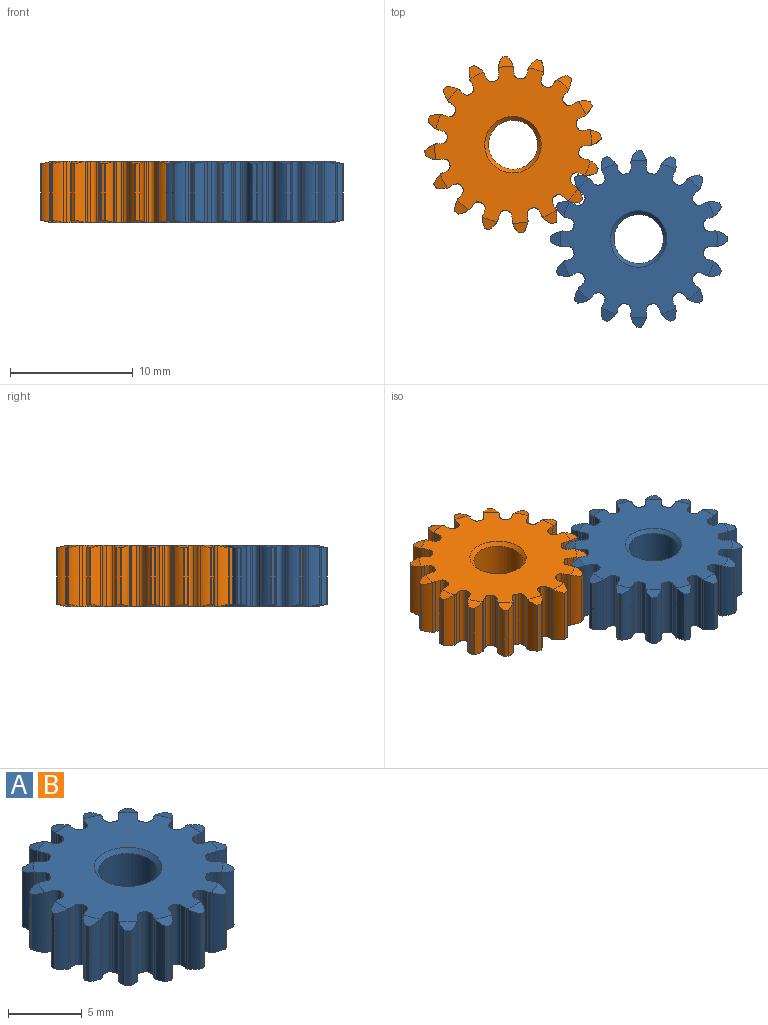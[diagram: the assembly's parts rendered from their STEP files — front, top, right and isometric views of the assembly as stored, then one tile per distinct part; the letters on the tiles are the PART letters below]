
ASSEMBLY  parts=2 mates=1
PART A: 229 faces, bbox 14.4x14.4x5 mm
  f0: plane 12.8x12.8mm, normal (0,0,-1), area 96.1mm2, adj f1,f2,f3,f4,f5,f6,f7,f8
  f1: cone r=9.2mm half-angle=75deg, axis (0,0,1), area 0.7mm2, adj f0,f17,f63,f64,f65,f208
  f2: cone r=9.2mm half-angle=75deg, axis (0,0,1), area 0.7mm2, adj f0,f60,f61,f62,f199,f200
  f3: cone r=9.2mm half-angle=75deg, axis (0,0,1), area 0.7mm2, adj f0,f57,f58,f59,f190,f191
  f4: cone r=9.2mm half-angle=75deg, axis (0,0,1), area 0.7mm2, adj f0,f54,f55,f56,f181,f182
  f5: cone r=9.2mm half-angle=75deg, axis (0,0,1), area 0.7mm2, adj f0,f51,f52,f53,f172,f173
  f6: cone r=9.2mm half-angle=75deg, axis (0,0,1), area 0.7mm2, adj f0,f48,f49,f50,f163,f164
  f7: cone r=9.2mm half-angle=75deg, axis (0,0,1), area 0.7mm2, adj f0,f45,f46,f47,f154,f155
  f8: cone r=9.2mm half-angle=75deg, axis (0,0,1), area 0.7mm2, adj f0,f42,f43,f44,f145,f146
  f9: cone r=9.2mm half-angle=75deg, axis (0,0,1), area 0.7mm2, adj f0,f39,f40,f41,f136,f137
  f10: cone r=9.2mm half-angle=75deg, axis (0,0,1), area 0.7mm2, adj f0,f36,f37,f38,f127,f128
  f11: cone r=9.2mm half-angle=75deg, axis (0,0,1), area 0.7mm2, adj f0,f33,f34,f35,f118,f119
  f12: cone r=9.2mm half-angle=75deg, axis (0,0,1), area 0.7mm2, adj f0,f30,f31,f32,f109,f110
  f13: cone r=9.2mm half-angle=75deg, axis (0,0,1), area 0.7mm2, adj f0,f27,f28,f29,f100,f101
  f14: cone r=9.2mm half-angle=75deg, axis (0,0,1), area 0.7mm2, adj f0,f24,f25,f26,f91,f92
  f15: cone r=9.2mm half-angle=75deg, axis (0,0,1), area 0.7mm2, adj f0,f21,f22,f23,f82,f83
  f16: cone r=9.2mm half-angle=75deg, axis (0,0,1), area 0.7mm2, adj f0,f18,f19,f20,f73,f74
  f17: cylinder r=0.08mm len=4.59mm, axis (0,0,-1), area 0.3mm2, adj f1,f64,f65,f225
  f18: cylinder r=0.08mm len=4.59mm, axis (0,0,-1), area 0.3mm2, adj f16,f19,f73,f210
  f19: cylinder r=7.2mm len=4.57mm, axis (0,0,-1), area 1.4mm2, adj f16,f18,f20,f210
  f20: cylinder r=0.08mm len=4.59mm, axis (0,0,-1), area 0.3mm2, adj f16,f19,f74,f210
  f21: cylinder r=0.08mm len=4.59mm, axis (0,0,-1), area 0.3mm2, adj f15,f22,f82,f211
  f22: cylinder r=7.2mm len=4.57mm, axis (0,0,-1), area 1.4mm2, adj f15,f21,f23,f211
  f23: cylinder r=0.08mm len=4.59mm, axis (0,0,-1), area 0.3mm2, adj f15,f22,f83,f211
  f24: cylinder r=0.08mm len=4.59mm, axis (0,0,-1), area 0.3mm2, adj f14,f25,f91,f212
  f25: cylinder r=7.2mm len=4.57mm, axis (0,0,-1), area 1.4mm2, adj f14,f24,f26,f212
  f26: cylinder r=0.08mm len=4.59mm, axis (0,0,-1), area 0.3mm2, adj f14,f25,f92,f212
  f27: cylinder r=0.08mm len=4.59mm, axis (0,0,-1), area 0.3mm2, adj f13,f28,f100,f213
  f28: cylinder r=7.2mm len=4.57mm, axis (0,0,-1), area 1.4mm2, adj f13,f27,f29,f213
  f29: cylinder r=0.08mm len=4.59mm, axis (0,0,-1), area 0.3mm2, adj f13,f28,f101,f213
  f30: cylinder r=0.08mm len=4.59mm, axis (0,0,-1), area 0.3mm2, adj f12,f31,f109,f214
  f31: cylinder r=7.2mm len=4.57mm, axis (0,0,-1), area 1.4mm2, adj f12,f30,f32,f214
  f32: cylinder r=0.08mm len=4.59mm, axis (0,0,-1), area 0.3mm2, adj f12,f31,f110,f214
  f33: cylinder r=0.08mm len=4.59mm, axis (0,0,-1), area 0.3mm2, adj f11,f34,f118,f215
  f34: cylinder r=7.2mm len=4.57mm, axis (0,0,-1), area 1.4mm2, adj f11,f33,f35,f215
  f35: cylinder r=0.08mm len=4.59mm, axis (0,0,-1), area 0.3mm2, adj f11,f34,f119,f215
  f36: cylinder r=0.08mm len=4.59mm, axis (0,0,-1), area 0.3mm2, adj f10,f37,f127,f216
  f37: cylinder r=7.2mm len=4.57mm, axis (0,0,-1), area 1.4mm2, adj f10,f36,f38,f216
  f38: cylinder r=0.08mm len=4.59mm, axis (0,0,-1), area 0.3mm2, adj f10,f37,f128,f216
  f39: cylinder r=0.08mm len=4.59mm, axis (0,0,-1), area 0.3mm2, adj f9,f40,f136,f217
  f40: cylinder r=7.2mm len=4.57mm, axis (0,0,-1), area 1.4mm2, adj f9,f39,f41,f217
  f41: cylinder r=0.08mm len=4.59mm, axis (0,0,-1), area 0.3mm2, adj f9,f40,f137,f217
  f42: cylinder r=0.08mm len=4.59mm, axis (0,0,-1), area 0.3mm2, adj f8,f43,f145,f218
  f43: cylinder r=7.2mm len=4.57mm, axis (0,0,-1), area 1.4mm2, adj f8,f42,f44,f218
  f44: cylinder r=0.08mm len=4.59mm, axis (0,0,-1), area 0.3mm2, adj f8,f43,f146,f218
  f45: cylinder r=0.08mm len=4.59mm, axis (0,0,-1), area 0.3mm2, adj f7,f46,f154,f219
  f46: cylinder r=7.2mm len=4.57mm, axis (0,0,-1), area 1.4mm2, adj f7,f45,f47,f219
  f47: cylinder r=0.08mm len=4.59mm, axis (0,0,-1), area 0.3mm2, adj f7,f46,f155,f219
  f48: cylinder r=0.08mm len=4.59mm, axis (0,0,-1), area 0.3mm2, adj f6,f49,f163,f220
  f49: cylinder r=7.2mm len=4.57mm, axis (0,0,-1), area 1.4mm2, adj f6,f48,f50,f220
  f50: cylinder r=0.08mm len=4.59mm, axis (0,0,-1), area 0.3mm2, adj f6,f49,f164,f220
  f51: cylinder r=0.08mm len=4.59mm, axis (0,0,-1), area 0.3mm2, adj f5,f52,f172,f221
  f52: cylinder r=7.2mm len=4.57mm, axis (0,0,-1), area 1.4mm2, adj f5,f51,f53,f221
  f53: cylinder r=0.08mm len=4.59mm, axis (0,0,-1), area 0.3mm2, adj f5,f52,f173,f221
  f54: cylinder r=0.08mm len=4.59mm, axis (0,0,-1), area 0.3mm2, adj f4,f55,f181,f222
  f55: cylinder r=7.2mm len=4.57mm, axis (0,0,-1), area 1.4mm2, adj f4,f54,f56,f222
  f56: cylinder r=0.08mm len=4.59mm, axis (0,0,-1), area 0.3mm2, adj f4,f55,f182,f222
  f57: cylinder r=0.08mm len=4.59mm, axis (0,0,-1), area 0.3mm2, adj f3,f58,f190,f223
  f58: cylinder r=7.2mm len=4.57mm, axis (0,0,-1), area 1.4mm2, adj f3,f57,f59,f223
  f59: cylinder r=0.08mm len=4.59mm, axis (0,0,-1), area 0.3mm2, adj f3,f58,f191,f223
  f60: cylinder r=0.08mm len=4.59mm, axis (0,0,-1), area 0.3mm2, adj f2,f61,f199,f224
  f61: cylinder r=7.2mm len=4.57mm, axis (0,0,-1), area 1.4mm2, adj f2,f60,f62,f224
  f62: cylinder r=0.08mm len=4.59mm, axis (0,0,-1), area 0.3mm2, adj f2,f61,f200,f224
  f63: cylinder r=0.08mm len=4.59mm, axis (0,0,-1), area 0.3mm2, adj f1,f64,f208,f225
  f64: cylinder r=7.2mm len=4.57mm, axis (0,0,-1), area 1.4mm2, adj f1,f17,f63,f225
  f65: cylinder r=2mm len=5mm, axis (0,0,-1), area 4.4mm2, adj f1,f17,f66,f225
  f66: cylinder r=0.65mm len=5mm, axis (0,0,-1), area 1.3mm2, adj f0,f65,f67,f209
  f67: cylinder r=1.6mm len=5mm, axis (0,0,-1), area 2.4mm2, adj f0,f66,f68,f209
  f68: cylinder r=0.4mm len=5mm, axis (0,0,-1), area 2.5mm2, adj f0,f67,f69,f209
  f69: cylinder r=5.4mm len=5mm, axis (0,0,-1), area 0.9mm2, adj f0,f68,f70,f209
  f70: cylinder r=0.4mm len=5mm, axis (0,0,-1), area 2.5mm2, adj f0,f69,f71,f209
  f71: cylinder r=1.6mm len=5mm, axis (0,0,-1), area 2.4mm2, adj f0,f70,f72,f209
  f72: cylinder r=0.65mm len=5mm, axis (0,0,-1), area 1.3mm2, adj f0,f71,f73,f209
  f73: cylinder r=2mm len=5mm, axis (0,0,-1), area 4.4mm2, adj f16,f18,f72,f210
  f74: cylinder r=2mm len=5mm, axis (0,0,-1), area 4.4mm2, adj f16,f20,f75,f210
  f75: cylinder r=0.65mm len=5mm, axis (0,0,-1), area 1.3mm2, adj f0,f74,f76,f209
  f76: cylinder r=1.6mm len=5mm, axis (0,0,-1), area 2.4mm2, adj f0,f75,f77,f209
  f77: cylinder r=0.4mm len=5mm, axis (0,0,-1), area 2.5mm2, adj f0,f76,f78,f209
  f78: cylinder r=5.4mm len=5mm, axis (0,0,-1), area 0.9mm2, adj f0,f77,f79,f209
  f79: cylinder r=0.4mm len=5mm, axis (0,0,-1), area 2.5mm2, adj f0,f78,f80,f209
  f80: cylinder r=1.6mm len=5mm, axis (0,0,-1), area 2.4mm2, adj f0,f79,f81,f209
  f81: cylinder r=0.65mm len=5mm, axis (0,0,-1), area 1.3mm2, adj f0,f80,f82,f209
  f82: cylinder r=2mm len=5mm, axis (0,0,-1), area 4.4mm2, adj f15,f21,f81,f211
  f83: cylinder r=2mm len=5mm, axis (0,0,-1), area 4.4mm2, adj f15,f23,f84,f211
  f84: cylinder r=0.65mm len=5mm, axis (0,0,-1), area 1.3mm2, adj f0,f83,f85,f209
  f85: cylinder r=1.6mm len=5mm, axis (0,0,-1), area 2.4mm2, adj f0,f84,f86,f209
  f86: cylinder r=0.4mm len=5mm, axis (0,0,-1), area 2.5mm2, adj f0,f85,f87,f209
  f87: cylinder r=5.4mm len=5mm, axis (0,0,-1), area 0.9mm2, adj f0,f86,f88,f209
  f88: cylinder r=0.4mm len=5mm, axis (0,0,-1), area 2.5mm2, adj f0,f87,f89,f209
  f89: cylinder r=1.6mm len=5mm, axis (0,0,-1), area 2.4mm2, adj f0,f88,f90,f209
  f90: cylinder r=0.65mm len=5mm, axis (0,0,-1), area 1.3mm2, adj f0,f89,f91,f209
  f91: cylinder r=2mm len=5mm, axis (0,0,-1), area 4.4mm2, adj f14,f24,f90,f212
  f92: cylinder r=2mm len=5mm, axis (0,0,-1), area 4.4mm2, adj f14,f26,f93,f212
  f93: cylinder r=0.65mm len=5mm, axis (0,0,-1), area 1.3mm2, adj f0,f92,f94,f209
  f94: cylinder r=1.6mm len=5mm, axis (0,0,-1), area 2.4mm2, adj f0,f93,f95,f209
  f95: cylinder r=0.4mm len=5mm, axis (0,0,-1), area 2.5mm2, adj f0,f94,f96,f209
  f96: cylinder r=5.4mm len=5mm, axis (0,0,-1), area 0.9mm2, adj f0,f95,f97,f209
  f97: cylinder r=0.4mm len=5mm, axis (0,0,-1), area 2.5mm2, adj f0,f96,f98,f209
  f98: cylinder r=1.6mm len=5mm, axis (0,0,-1), area 2.4mm2, adj f0,f97,f99,f209
  f99: cylinder r=0.65mm len=5mm, axis (0,0,-1), area 1.3mm2, adj f0,f98,f100,f209
  f100: cylinder r=2mm len=5mm, axis (0,0,-1), area 4.4mm2, adj f13,f27,f99,f213
  f101: cylinder r=2mm len=5mm, axis (0,0,-1), area 4.4mm2, adj f13,f29,f102,f213
  f102: cylinder r=0.65mm len=5mm, axis (0,0,-1), area 1.3mm2, adj f0,f101,f103,f209
  f103: cylinder r=1.6mm len=5mm, axis (0,0,-1), area 2.4mm2, adj f0,f102,f104,f209
  f104: cylinder r=0.4mm len=5mm, axis (0,0,-1), area 2.5mm2, adj f0,f103,f105,f209
  f105: cylinder r=5.4mm len=5mm, axis (0,0,-1), area 0.9mm2, adj f0,f104,f106,f209
  f106: cylinder r=0.4mm len=5mm, axis (0,0,-1), area 2.5mm2, adj f0,f105,f107,f209
  f107: cylinder r=1.6mm len=5mm, axis (0,0,-1), area 2.4mm2, adj f0,f106,f108,f209
  f108: cylinder r=0.65mm len=5mm, axis (0,0,-1), area 1.3mm2, adj f0,f107,f109,f209
  f109: cylinder r=2mm len=5mm, axis (0,0,-1), area 4.4mm2, adj f12,f30,f108,f214
  f110: cylinder r=2mm len=5mm, axis (0,0,-1), area 4.4mm2, adj f12,f32,f111,f214
  f111: cylinder r=0.65mm len=5mm, axis (0,0,-1), area 1.3mm2, adj f0,f110,f112,f209
  f112: cylinder r=1.6mm len=5mm, axis (0,0,-1), area 2.4mm2, adj f0,f111,f113,f209
  f113: cylinder r=0.4mm len=5mm, axis (0,0,-1), area 2.5mm2, adj f0,f112,f114,f209
  f114: cylinder r=5.4mm len=5mm, axis (0,0,-1), area 0.9mm2, adj f0,f113,f115,f209
  f115: cylinder r=0.4mm len=5mm, axis (0,0,-1), area 2.5mm2, adj f0,f114,f116,f209
  f116: cylinder r=1.6mm len=5mm, axis (0,0,-1), area 2.4mm2, adj f0,f115,f117,f209
  f117: cylinder r=0.65mm len=5mm, axis (0,0,-1), area 1.3mm2, adj f0,f116,f118,f209
  f118: cylinder r=2mm len=5mm, axis (0,0,-1), area 4.4mm2, adj f11,f33,f117,f215
  f119: cylinder r=2mm len=5mm, axis (0,0,-1), area 4.4mm2, adj f11,f35,f120,f215
  f120: cylinder r=0.65mm len=5mm, axis (0,0,-1), area 1.3mm2, adj f0,f119,f121,f209
  f121: cylinder r=1.6mm len=5mm, axis (0,0,-1), area 2.4mm2, adj f0,f120,f122,f209
  f122: cylinder r=0.4mm len=5mm, axis (0,0,-1), area 2.5mm2, adj f0,f121,f123,f209
  f123: cylinder r=5.4mm len=5mm, axis (0,0,-1), area 0.9mm2, adj f0,f122,f124,f209
  f124: cylinder r=0.4mm len=5mm, axis (0,0,-1), area 2.5mm2, adj f0,f123,f125,f209
  f125: cylinder r=1.6mm len=5mm, axis (0,0,-1), area 2.4mm2, adj f0,f124,f126,f209
  f126: cylinder r=0.65mm len=5mm, axis (0,0,-1), area 1.3mm2, adj f0,f125,f127,f209
  f127: cylinder r=2mm len=5mm, axis (0,0,-1), area 4.4mm2, adj f10,f36,f126,f216
  f128: cylinder r=2mm len=5mm, axis (0,0,-1), area 4.4mm2, adj f10,f38,f129,f216
  f129: cylinder r=0.65mm len=5mm, axis (0,0,-1), area 1.3mm2, adj f0,f128,f130,f209
  f130: cylinder r=1.6mm len=5mm, axis (0,0,-1), area 2.4mm2, adj f0,f129,f131,f209
  f131: cylinder r=0.4mm len=5mm, axis (0,0,-1), area 2.5mm2, adj f0,f130,f132,f209
  f132: cylinder r=5.4mm len=5mm, axis (0,0,-1), area 0.9mm2, adj f0,f131,f133,f209
  f133: cylinder r=0.4mm len=5mm, axis (0,0,-1), area 2.5mm2, adj f0,f132,f134,f209
  f134: cylinder r=1.6mm len=5mm, axis (0,0,-1), area 2.4mm2, adj f0,f133,f135,f209
  f135: cylinder r=0.65mm len=5mm, axis (0,0,-1), area 1.3mm2, adj f0,f134,f136,f209
  f136: cylinder r=2mm len=5mm, axis (0,0,-1), area 4.4mm2, adj f9,f39,f135,f217
  f137: cylinder r=2mm len=5mm, axis (0,0,-1), area 4.4mm2, adj f9,f41,f138,f217
  f138: cylinder r=0.65mm len=5mm, axis (0,0,-1), area 1.3mm2, adj f0,f137,f139,f209
  f139: cylinder r=1.6mm len=5mm, axis (0,0,-1), area 2.4mm2, adj f0,f138,f140,f209
  f140: cylinder r=0.4mm len=5mm, axis (0,0,-1), area 2.5mm2, adj f0,f139,f141,f209
  f141: cylinder r=5.4mm len=5mm, axis (0,0,-1), area 0.9mm2, adj f0,f140,f142,f209
  f142: cylinder r=0.4mm len=5mm, axis (0,0,-1), area 2.5mm2, adj f0,f141,f143,f209
  f143: cylinder r=1.6mm len=5mm, axis (0,0,-1), area 2.4mm2, adj f0,f142,f144,f209
  f144: cylinder r=0.65mm len=5mm, axis (0,0,-1), area 1.3mm2, adj f0,f143,f145,f209
  f145: cylinder r=2mm len=5mm, axis (0,0,-1), area 4.4mm2, adj f8,f42,f144,f218
  f146: cylinder r=2mm len=5mm, axis (0,0,-1), area 4.4mm2, adj f8,f44,f147,f218
  f147: cylinder r=0.65mm len=5mm, axis (0,0,-1), area 1.3mm2, adj f0,f146,f148,f209
  f148: cylinder r=1.6mm len=5mm, axis (0,0,-1), area 2.4mm2, adj f0,f147,f149,f209
  f149: cylinder r=0.4mm len=5mm, axis (0,0,-1), area 2.5mm2, adj f0,f148,f150,f209
  f150: cylinder r=5.4mm len=5mm, axis (0,0,-1), area 0.9mm2, adj f0,f149,f151,f209
  f151: cylinder r=0.4mm len=5mm, axis (0,0,-1), area 2.5mm2, adj f0,f150,f152,f209
  f152: cylinder r=1.6mm len=5mm, axis (0,0,-1), area 2.4mm2, adj f0,f151,f153,f209
  f153: cylinder r=0.65mm len=5mm, axis (0,0,-1), area 1.3mm2, adj f0,f152,f154,f209
  f154: cylinder r=2mm len=5mm, axis (0,0,-1), area 4.4mm2, adj f7,f45,f153,f219
  f155: cylinder r=2mm len=5mm, axis (0,0,-1), area 4.4mm2, adj f7,f47,f156,f219
  f156: cylinder r=0.65mm len=5mm, axis (0,0,-1), area 1.3mm2, adj f0,f155,f157,f209
  f157: cylinder r=1.6mm len=5mm, axis (0,0,-1), area 2.4mm2, adj f0,f156,f158,f209
  f158: cylinder r=0.4mm len=5mm, axis (0,0,-1), area 2.5mm2, adj f0,f157,f159,f209
  f159: cylinder r=5.4mm len=5mm, axis (0,0,-1), area 0.9mm2, adj f0,f158,f160,f209
  f160: cylinder r=0.4mm len=5mm, axis (0,0,-1), area 2.5mm2, adj f0,f159,f161,f209
  f161: cylinder r=1.6mm len=5mm, axis (0,0,-1), area 2.4mm2, adj f0,f160,f162,f209
  f162: cylinder r=0.65mm len=5mm, axis (0,0,-1), area 1.3mm2, adj f0,f161,f163,f209
  f163: cylinder r=2mm len=5mm, axis (0,0,-1), area 4.4mm2, adj f6,f48,f162,f220
  f164: cylinder r=2mm len=5mm, axis (0,0,-1), area 4.4mm2, adj f6,f50,f165,f220
  f165: cylinder r=0.65mm len=5mm, axis (0,0,-1), area 1.3mm2, adj f0,f164,f166,f209
  f166: cylinder r=1.6mm len=5mm, axis (0,0,-1), area 2.4mm2, adj f0,f165,f167,f209
  f167: cylinder r=0.4mm len=5mm, axis (0,0,-1), area 2.5mm2, adj f0,f166,f168,f209
  f168: cylinder r=5.4mm len=5mm, axis (0,0,-1), area 0.9mm2, adj f0,f167,f169,f209
  f169: cylinder r=0.4mm len=5mm, axis (0,0,-1), area 2.5mm2, adj f0,f168,f170,f209
  f170: cylinder r=1.6mm len=5mm, axis (0,0,-1), area 2.4mm2, adj f0,f169,f171,f209
  f171: cylinder r=0.65mm len=5mm, axis (0,0,-1), area 1.3mm2, adj f0,f170,f172,f209
  f172: cylinder r=2mm len=5mm, axis (0,0,-1), area 4.4mm2, adj f5,f51,f171,f221
  f173: cylinder r=2mm len=5mm, axis (0,0,-1), area 4.4mm2, adj f5,f53,f174,f221
  f174: cylinder r=0.65mm len=5mm, axis (0,0,-1), area 1.3mm2, adj f0,f173,f175,f209
  f175: cylinder r=1.6mm len=5mm, axis (0,0,-1), area 2.4mm2, adj f0,f174,f176,f209
  f176: cylinder r=0.4mm len=5mm, axis (0,0,-1), area 2.5mm2, adj f0,f175,f177,f209
  f177: cylinder r=5.4mm len=5mm, axis (0,0,-1), area 0.9mm2, adj f0,f176,f178,f209
  f178: cylinder r=0.4mm len=5mm, axis (0,0,-1), area 2.5mm2, adj f0,f177,f179,f209
  f179: cylinder r=1.6mm len=5mm, axis (0,0,-1), area 2.4mm2, adj f0,f178,f180,f209
  f180: cylinder r=0.65mm len=5mm, axis (0,0,-1), area 1.3mm2, adj f0,f179,f181,f209
  f181: cylinder r=2mm len=5mm, axis (0,0,-1), area 4.4mm2, adj f4,f54,f180,f222
  f182: cylinder r=2mm len=5mm, axis (0,0,-1), area 4.4mm2, adj f4,f56,f183,f222
  f183: cylinder r=0.65mm len=5mm, axis (0,0,-1), area 1.3mm2, adj f0,f182,f184,f209
  f184: cylinder r=1.6mm len=5mm, axis (0,0,-1), area 2.4mm2, adj f0,f183,f185,f209
  f185: cylinder r=0.4mm len=5mm, axis (0,0,-1), area 2.5mm2, adj f0,f184,f186,f209
  f186: cylinder r=5.4mm len=5mm, axis (0,0,-1), area 0.9mm2, adj f0,f185,f187,f209
  f187: cylinder r=0.4mm len=5mm, axis (0,0,-1), area 2.5mm2, adj f0,f186,f188,f209
  f188: cylinder r=1.6mm len=5mm, axis (0,0,-1), area 2.4mm2, adj f0,f187,f189,f209
  f189: cylinder r=0.65mm len=5mm, axis (0,0,-1), area 1.3mm2, adj f0,f188,f190,f209
  f190: cylinder r=2mm len=5mm, axis (0,0,-1), area 4.4mm2, adj f3,f57,f189,f223
  f191: cylinder r=2mm len=5mm, axis (0,0,-1), area 4.4mm2, adj f3,f59,f192,f223
  f192: cylinder r=0.65mm len=5mm, axis (0,0,-1), area 1.3mm2, adj f0,f191,f193,f209
  f193: cylinder r=1.6mm len=5mm, axis (0,0,-1), area 2.4mm2, adj f0,f192,f194,f209
  f194: cylinder r=0.4mm len=5mm, axis (0,0,-1), area 2.5mm2, adj f0,f193,f195,f209
  f195: cylinder r=5.4mm len=5mm, axis (0,0,-1), area 0.9mm2, adj f0,f194,f196,f209
  f196: cylinder r=0.4mm len=5mm, axis (0,0,-1), area 2.5mm2, adj f0,f195,f197,f209
  f197: cylinder r=1.6mm len=5mm, axis (0,0,-1), area 2.4mm2, adj f0,f196,f198,f209
  f198: cylinder r=0.65mm len=5mm, axis (0,0,-1), area 1.3mm2, adj f0,f197,f199,f209
  f199: cylinder r=2mm len=5mm, axis (0,0,-1), area 4.4mm2, adj f2,f60,f198,f224
  f200: cylinder r=2mm len=5mm, axis (0,0,-1), area 4.4mm2, adj f2,f62,f201,f224
  f201: cylinder r=0.65mm len=5mm, axis (0,0,-1), area 1.3mm2, adj f0,f200,f202,f209
  f202: cylinder r=1.6mm len=5mm, axis (0,0,-1), area 2.4mm2, adj f0,f201,f203,f209
  f203: cylinder r=0.4mm len=5mm, axis (0,0,-1), area 2.5mm2, adj f0,f202,f204,f209
  f204: cylinder r=5.4mm len=5mm, axis (0,0,-1), area 0.9mm2, adj f0,f203,f205,f209
  f205: cylinder r=0.4mm len=5mm, axis (0,0,-1), area 2.5mm2, adj f0,f204,f206,f209
  f206: cylinder r=1.6mm len=5mm, axis (0,0,-1), area 2.4mm2, adj f0,f205,f207,f209
  f207: cylinder r=0.65mm len=5mm, axis (0,0,-1), area 1.3mm2, adj f0,f206,f208,f209
  f208: cylinder r=2mm len=5mm, axis (0,0,-1), area 4.4mm2, adj f1,f63,f207,f225
  f209: plane 12.8x12.8mm, normal (0,0,1), area 96.1mm2, adj f66,f67,f68,f69,f70,f71,f72,f75
  f210: cone r=6.4mm half-angle=75deg, axis (0,0,-1), area 0.7mm2, adj f18,f19,f20,f73,f74,f209
  f211: cone r=6.4mm half-angle=75deg, axis (0,0,-1), area 0.7mm2, adj f21,f22,f23,f82,f83,f209
  f212: cone r=6.4mm half-angle=75deg, axis (0,0,-1), area 0.7mm2, adj f24,f25,f26,f91,f92,f209
  f213: cone r=6.4mm half-angle=75deg, axis (0,0,-1), area 0.7mm2, adj f27,f28,f29,f100,f101,f209
  f214: cone r=6.4mm half-angle=75deg, axis (0,0,-1), area 0.7mm2, adj f30,f31,f32,f109,f110,f209
  f215: cone r=6.4mm half-angle=75deg, axis (0,0,-1), area 0.7mm2, adj f33,f34,f35,f118,f119,f209
  f216: cone r=6.4mm half-angle=75deg, axis (0,0,-1), area 0.7mm2, adj f36,f37,f38,f127,f128,f209
  f217: cone r=6.4mm half-angle=75deg, axis (0,0,-1), area 0.7mm2, adj f39,f40,f41,f136,f137,f209
  f218: cone r=6.4mm half-angle=75deg, axis (0,0,-1), area 0.7mm2, adj f42,f43,f44,f145,f146,f209
  f219: cone r=6.4mm half-angle=75deg, axis (0,0,-1), area 0.7mm2, adj f45,f46,f47,f154,f155,f209
  f220: cone r=6.4mm half-angle=75deg, axis (0,0,-1), area 0.7mm2, adj f48,f49,f50,f163,f164,f209
  f221: cone r=6.4mm half-angle=75deg, axis (0,0,-1), area 0.7mm2, adj f51,f52,f53,f172,f173,f209
  f222: cone r=6.4mm half-angle=75deg, axis (0,0,-1), area 0.7mm2, adj f54,f55,f56,f181,f182,f209
  f223: cone r=6.4mm half-angle=75deg, axis (0,0,-1), area 0.7mm2, adj f57,f58,f59,f190,f191,f209
  f224: cone r=6.4mm half-angle=75deg, axis (0,0,-1), area 0.7mm2, adj f60,f61,f62,f199,f200,f209
  f225: cone r=6.4mm half-angle=75deg, axis (0,0,-1), area 0.7mm2, adj f17,f63,f64,f65,f208,f209
  f226: cylinder r=2mm len=4.4mm, axis (0,0,-1), area 55.3mm2, adj f227,f228
  f227: cone r=2.3mm half-angle=45deg, axis (0,0,-1), area 5.7mm2, adj f0,f226
  f228: cone r=2mm half-angle=45deg, axis (0,0,1), area 5.7mm2, adj f209,f226
PART B: same geometry as A
PLACE A at identity fixed
PLACE B rot(axis=(0,0,-1),107.2deg) t=(-10.24,7.67,0)mm
MATE planar B.f1 <-> A.f1  axis (0,0,1) through (-10.24,7.67,5)mm
